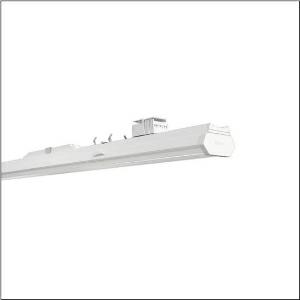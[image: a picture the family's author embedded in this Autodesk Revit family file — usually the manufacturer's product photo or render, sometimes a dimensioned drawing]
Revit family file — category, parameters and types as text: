
# Revit family: licross_r__11_protected_mo_51tp11dn495g_6ace
name_source: partatom
category: Lighting Fixtures
units: mm (PartAtom-declared; Revit-internal decimal feet)

## family parameters
Cut with Voids When Loaded = No
Host = Face
Light Source = No
Part Type = Normal
Room Calculation Point = No
Round Connector Dimension = Use Diameter
Shared = No

## types (1)
- --- (1 x LED, 9930 lm, 57.1 W, 4000K)
    Apparent Load = 57 VA
    CIE Flux Codes = 83 94 98 100 100
    Color Rendering = 80
    Color Temperature = 4000K
    Default Elevation = 1800 mm
    Description = Licross® 11 Protected MO, luminaire insert, of sheet steel, galvanised, coil coated, white, length: 1.500mm, width: 90mm, height: 101mm, LED rated luminous flux: 9.980lm, light colour: 840, control gear: DALI 2, with plug, 5-pole, with phase selection, mains connection: 220..240V, AC, 50/60Hz, rated input power: 57W, halogen-free wiring, primary light control with lens, of plastic, primary optical cover: cover, of PMMA, light emission: direct distribution, primary light characteristic: symmetric, protection rating (complete): IP64, insulation class (complete): insulation class I (protective earthing), certification: CE, ENEC, VDE, UKCA, protection symbol: D if used in an environment with conductive dust loads with corresponding accessories, impact resistance: IK06, permissible ambient temperature for indoor applications: -25..+35°C, corresponds to IFS (International Featured Standards) requirements for safety and quality in the food industry, reducing of maximum allowable ambient temperature of 5°C with ceiling mounting, LABS conformity tested according to VDMA 24364:2018-05, packaging unit: 1 piece
    Height = 92 mm
    Lamp = 1 x LED
    Lamp Light Flux = 9930 lm
    Lamp Power = 57.1 W
    Lamp count = 1
    Length = 1500 mm
    Luminous efficacy = 174 lm/W
    Manufacturer = Siteco
    ModVariant = No
    Model = 51TP11DN495G
    Mounting Place = Ceiling
    Mounting Type = Pendant
    Number of Poles = 1
    OnlyDefault = Yes
    Power Factor = 1
    Product Name = Licross® 11 Protected MO
    Product group = luminaire insert
    ProductGroupID = 902
    Protection Class = Protection class I
    Protection Degree = IP 64
    RLX_Detail_Level = 1
    RLX_Emergency_Light_Flux = 0 lm
    RLX_Emergency_Type = 0
    RLX_Emergency_Type_DB = No
    RlxData = <blob elided: 24081 chars, md5=3777be6a>
    Socket = socket
    Standby Power = 0 W
    System Light Flux = 9930 lm
    System Power = 57 W
    Type Comments = factory setting: luminous flux: 100 % | dim-lin: 254 | 378 mA
    Type Image = l_1256148.jpg
    URL = http://relux.com
    VarID = @adj_100972
    Voltage = 0 V
    Weight = 0.00 kg
    Width = 88 mm

## geometry (parser evidence)
native form markers: Blend x4, Sweep x11
no freeform markers — native parametric forms only
